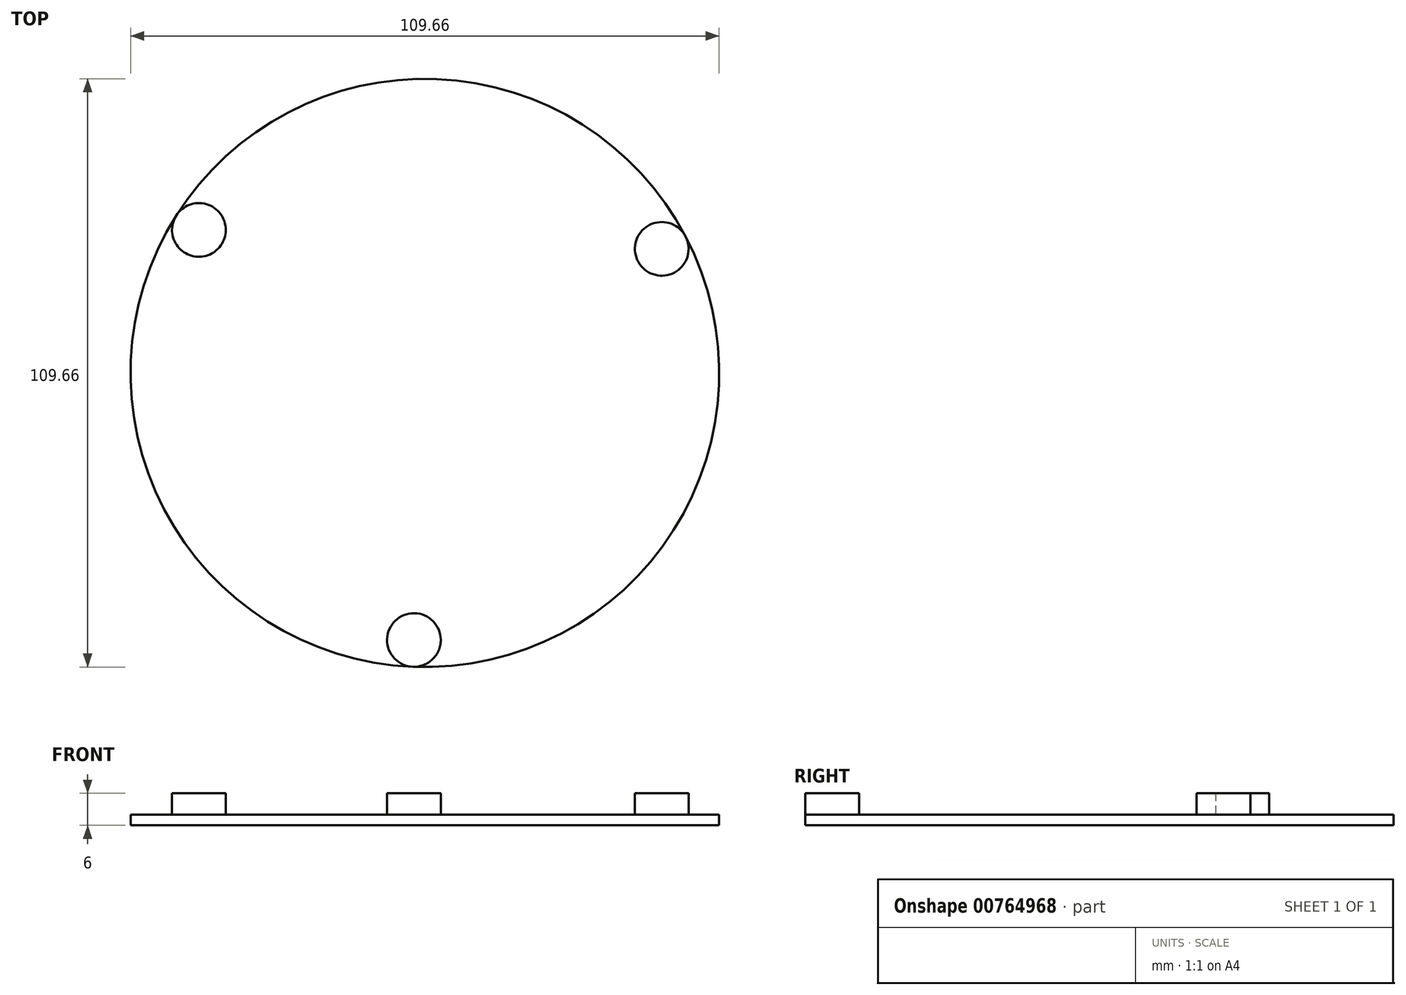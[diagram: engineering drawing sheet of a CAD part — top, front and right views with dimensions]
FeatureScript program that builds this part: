
annotation { "Feature Type Name" : "Feature", "Feature Type Description" : "" }
export const myFeature = defineFeature(function(context is Context, id is Id, definition is map)
    precondition{}
    {
        {
            var Q0;
            Q0=qCreatedBy(makeId("Top.planeOp"),FACE);
            var sketch = newSketch(context, id + "F0", { "sketchPlane" : qUnion([Q0])});
            skCircle(sketch, "E0", {"center": v(0, 0) * mm, "radius": 54.83 * mm});
            skSolve(sketch);
        }
        {
            var Q0;
            Q0=makeQuery(id+"F0.imprint","IMPRINT",FACE,{"disambiguationData":[TD([[makeQuery(id+"F0.imprint","IMPRINT",EDGE,{"derivedFrom":sQuery(id+"F0.wireOp",EDGE,"E0")}),1.0]])]});
            extrude(context, id + "F1", {"entities" : qUnion([Q0]), "depth" : 2 * mm, "offsetDistance" : 25 * mm});
        }
        {
            var Q0;
            Q0=makeQuery(id+"F1.opExtrude","CAP_FACE",FACE,{"disambiguationData":[OSD([sQuery(id+"F0.wireOp",EDGE,"E0")])],"isStart":false});
            var sketch = newSketch(context, id + "F2", { "sketchPlane" : qUnion([Q0])});
            skCircle(sketch, "E1.0", {"center": v(0, 0) * mm, "radius": 49.83 * mm});
            skCircle(sketch, "E2.cCircle", {"center": v(0, 0) * mm, "radius": 49.83 * mm, "construction": true});
            skLineSegment(sketch, "E2.0", {"start": v(44.13, 23.13) * mm, "end": v(-2.04, -49.79) * mm});
            skLineSegment(sketch, "E2.1", {"start": v(-2.04, -49.79) * mm, "end": v(-42.1, 26.66) * mm});
            skLineSegment(sketch, "E2.2", {"start": v(-42.1, 26.66) * mm, "end": v(44.13, 23.13) * mm});
            skCircle(sketch, "E3", {"center": v(-42.1, 26.66) * mm, "radius": 5 * mm});
            skCircle(sketch, "E4", {"center": v(-2.04, -49.79) * mm, "radius": 5 * mm});
            skCircle(sketch, "E5", {"center": v(44.13, 23.13) * mm, "radius": 5 * mm});
            skSolve(sketch);
        }
        {
            var Q0;
            {var subQ0=sQuery(id+"F2.wireOp",EDGE,"E1.0");var subQ2=sQuery(id+"F2.wireOp",EDGE,"E3");var subQ3=makeQuery(id+"F2.imprint","INTERSECT",VERTEX,{"disambiguationData":[OD(0.0)],"derivedFrom":[subQ0,subQ2]});Q0=makeQuery(id+"F2.imprint","IMPRINT",FACE,{"disambiguationData":[TD([[makeQuery(id+"F2.imprint","IMPRINT",EDGE,{"disambiguationData":[TD([[subQ3,-1.0]])],"derivedFrom":subQ2}),1.0]])]});}
            var Q1;
            {var subQ1=sQuery(id+"F2.wireOp",EDGE,"E1.0");var subQ3=sQuery(id+"F2.wireOp",EDGE,"E3");var subQ4=makeQuery(id+"F2.imprint","INTERSECT",VERTEX,{"disambiguationData":[OD(1.0)],"derivedFrom":[subQ1,subQ3]});Q1=makeQuery(id+"F2.imprint","IMPRINT",FACE,{"disambiguationData":[TD([[makeQuery(id+"F2.imprint","IMPRINT",EDGE,{"disambiguationData":[TD([[subQ4,-1.0]])],"derivedFrom":subQ3}),1.0]])]});}
            var Q2;
            {var subQ1=sQuery(id+"F2.wireOp",EDGE,"E1.0");var subQ3=sQuery(id+"F2.wireOp",EDGE,"E3");var subQ4=makeQuery(id+"F2.imprint","INTERSECT",VERTEX,{"disambiguationData":[OD(0.0)],"derivedFrom":[subQ1,subQ3]});Q2=makeQuery(id+"F2.imprint","IMPRINT",FACE,{"disambiguationData":[TD([[makeQuery(id+"F2.imprint","IMPRINT",EDGE,{"disambiguationData":[TD([[subQ4,1.0]])],"derivedFrom":subQ3}),1.0]])]});}
            var Q3;
            {var subQ1=sQuery(id+"F2.wireOp",EDGE,"E2.1");var subQ3=sQuery(id+"F2.wireOp",EDGE,"E3");var subQ4=makeQuery(id+"F2.imprint","INTERSECT",VERTEX,{"derivedFrom":[subQ1,subQ3]});Q3=makeQuery(id+"F2.imprint","IMPRINT",FACE,{"disambiguationData":[TD([[makeQuery(id+"F2.imprint","IMPRINT",EDGE,{"disambiguationData":[TD([[subQ4,-1.0]])],"derivedFrom":subQ3}),1.0]])]});}
            var Q4;
            {var subQ0=sQuery(id+"F2.wireOp",EDGE,"E1.0");var subQ2=sQuery(id+"F2.wireOp",EDGE,"E5");var subQ4=makeQuery(id+"F2.imprint","INTERSECT",VERTEX,{"disambiguationData":[OD(1.0)],"derivedFrom":[subQ0,subQ2]});Q4=makeQuery(id+"F2.imprint","IMPRINT",FACE,{"disambiguationData":[TD([[makeQuery(id+"F2.imprint","IMPRINT",EDGE,{"disambiguationData":[TD([[subQ4,1.0]])],"derivedFrom":subQ2}),1.0]])]});}
            var Q5;
            {var subQ1=sQuery(id+"F2.wireOp",EDGE,"E1.0");var subQ3=sQuery(id+"F2.wireOp",EDGE,"E5");var subQ4=makeQuery(id+"F2.imprint","INTERSECT",VERTEX,{"disambiguationData":[OD(1.0)],"derivedFrom":[subQ1,subQ3]});Q5=makeQuery(id+"F2.imprint","IMPRINT",FACE,{"disambiguationData":[TD([[makeQuery(id+"F2.imprint","IMPRINT",EDGE,{"disambiguationData":[TD([[subQ4,-1.0]])],"derivedFrom":subQ3}),1.0]])]});}
            var Q6;
            {var subQ1=sQuery(id+"F2.wireOp",EDGE,"E2.0");var subQ3=sQuery(id+"F2.wireOp",EDGE,"E5");var subQ4=makeQuery(id+"F2.imprint","INTERSECT",VERTEX,{"derivedFrom":[subQ1,subQ3]});Q6=makeQuery(id+"F2.imprint","IMPRINT",FACE,{"disambiguationData":[TD([[makeQuery(id+"F2.imprint","IMPRINT",EDGE,{"disambiguationData":[TD([[subQ4,1.0]])],"derivedFrom":subQ3}),1.0]])]});}
            var Q7;
            {var subQ1=sQuery(id+"F2.wireOp",EDGE,"E1.0");var subQ3=sQuery(id+"F2.wireOp",EDGE,"E5");var subQ4=makeQuery(id+"F2.imprint","INTERSECT",VERTEX,{"disambiguationData":[OD(0.0)],"derivedFrom":[subQ1,subQ3]});Q7=makeQuery(id+"F2.imprint","IMPRINT",FACE,{"disambiguationData":[TD([[makeQuery(id+"F2.imprint","IMPRINT",EDGE,{"disambiguationData":[TD([[subQ4,1.0]])],"derivedFrom":subQ3}),1.0]])]});}
            var Q8;
            {var subQ1=sQuery(id+"F2.wireOp",EDGE,"E1.0");var subQ3=sQuery(id+"F2.wireOp",EDGE,"E4");var subQ4=makeQuery(id+"F2.imprint","INTERSECT",VERTEX,{"disambiguationData":[OD(0.0)],"derivedFrom":[subQ1,subQ3]});Q8=makeQuery(id+"F2.imprint","IMPRINT",FACE,{"disambiguationData":[TD([[makeQuery(id+"F2.imprint","IMPRINT",EDGE,{"disambiguationData":[TD([[subQ4,1.0]])],"derivedFrom":subQ3}),1.0]])]});}
            var Q9;
            {var subQ1=sQuery(id+"F2.wireOp",EDGE,"E2.0");var subQ3=sQuery(id+"F2.wireOp",EDGE,"E4");var subQ4=makeQuery(id+"F2.imprint","INTERSECT",VERTEX,{"derivedFrom":[subQ1,subQ3]});Q9=makeQuery(id+"F2.imprint","IMPRINT",FACE,{"disambiguationData":[TD([[makeQuery(id+"F2.imprint","IMPRINT",EDGE,{"disambiguationData":[TD([[subQ4,-1.0]])],"derivedFrom":subQ3}),1.0]])]});}
            var Q10;
            {var subQ0=sQuery(id+"F2.wireOp",EDGE,"E1.0");var subQ2=sQuery(id+"F2.wireOp",EDGE,"E4");var subQ3=makeQuery(id+"F2.imprint","INTERSECT",VERTEX,{"disambiguationData":[OD(0.0)],"derivedFrom":[subQ0,subQ2]});Q10=makeQuery(id+"F2.imprint","IMPRINT",FACE,{"disambiguationData":[TD([[makeQuery(id+"F2.imprint","IMPRINT",EDGE,{"disambiguationData":[TD([[subQ3,-1.0]])],"derivedFrom":subQ2}),1.0]])]});}
            var Q11;
            {var subQ1=sQuery(id+"F2.wireOp",EDGE,"E1.0");var subQ3=sQuery(id+"F2.wireOp",EDGE,"E4");var subQ4=makeQuery(id+"F2.imprint","INTERSECT",VERTEX,{"disambiguationData":[OD(1.0)],"derivedFrom":[subQ1,subQ3]});Q11=makeQuery(id+"F2.imprint","IMPRINT",FACE,{"disambiguationData":[TD([[makeQuery(id+"F2.imprint","IMPRINT",EDGE,{"disambiguationData":[TD([[subQ4,-1.0]])],"derivedFrom":subQ3}),1.0]])]});}
            var Q12;
            Q12=sQuery(id+"F2.wireOp",EDGE,"E5");
            var Q13;
            Q13=sQuery(id+"F2.wireOp",EDGE,"E4");
            var Q14;
            Q14=sQuery(id+"F2.wireOp",EDGE,"E3");
            extrude(context, id + "F3", {"entities" : qUnion([Q0, Q1, Q2, Q3, Q4, Q5, Q6, Q7, Q8, Q9, Q10, Q11]), "operationType" : NewBodyOperationType.ADD, "surfaceEntities" : qUnion([Q12, Q13, Q14]), "depth" : 4 * mm, "offsetDistance" : 25 * mm});
        }
    });
